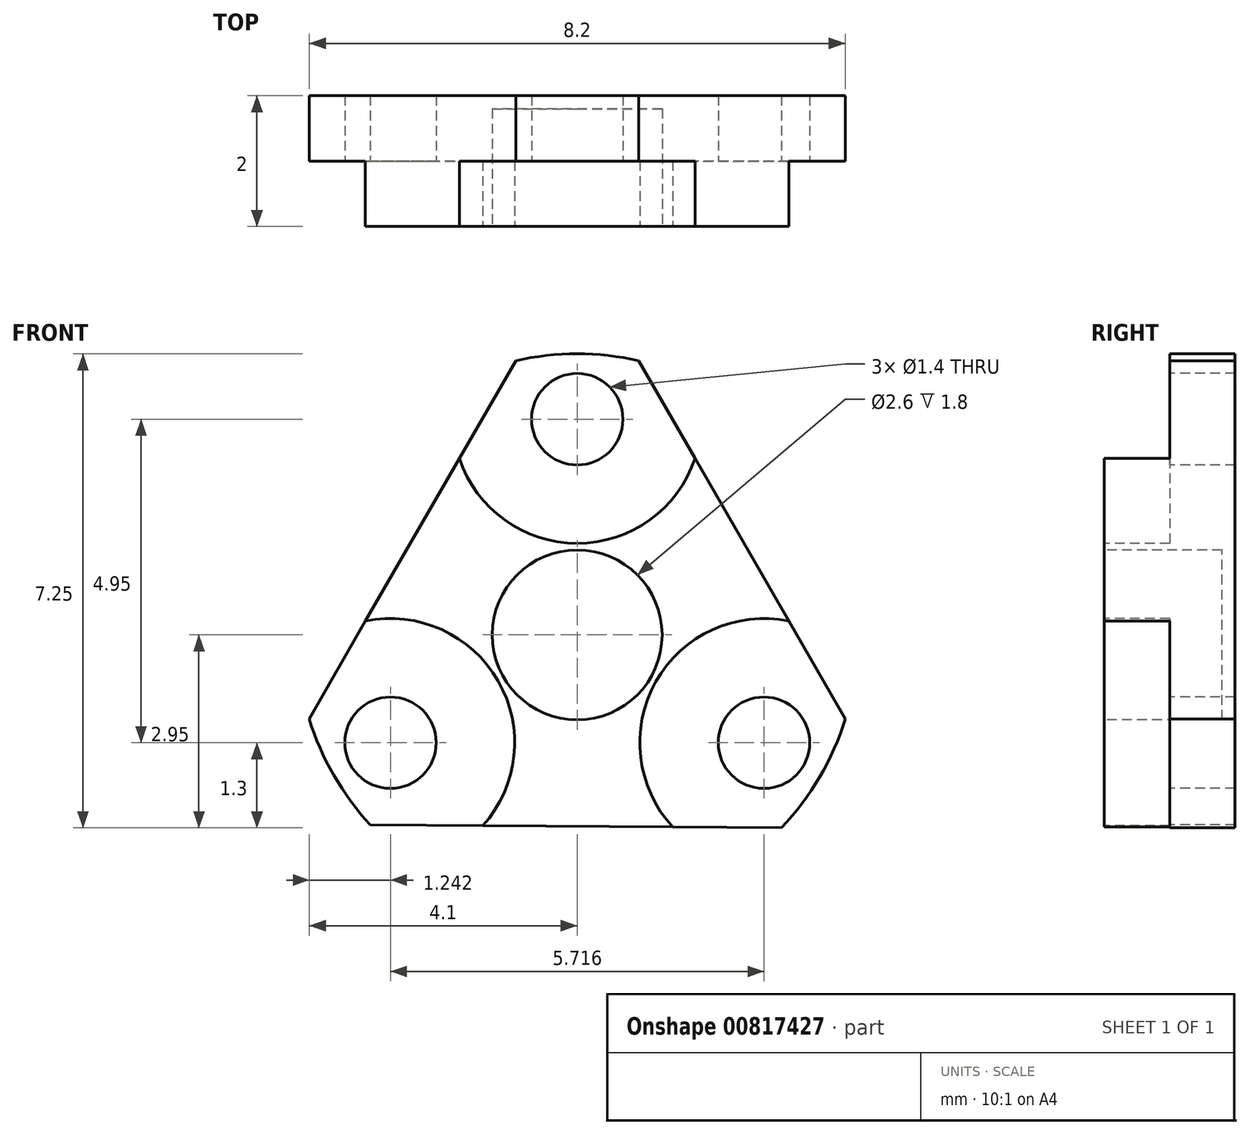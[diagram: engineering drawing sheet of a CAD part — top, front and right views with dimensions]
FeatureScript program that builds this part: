
annotation { "Feature Type Name" : "Feature", "Feature Type Description" : "" }
export const myFeature = defineFeature(function(context is Context, id is Id, definition is map)
    precondition{}
    {
        {
            var Q0;
            Q0=qCreatedBy(makeId("Front.planeOp"),FACE);
            var sketch = newSketch(context, id + "F0", { "sketchPlane" : qUnion([Q0])});
            skCircle(sketch, "E0", {"center": v(0, 0) * mm, "radius": 4.3 * mm});
            skSolve(sketch);
        }
        {
            var Q0;
            Q0=makeQuery(id+"F0.imprint","IMPRINT",FACE,{"disambiguationData":[TD([[makeQuery(id+"F0.imprint","IMPRINT",EDGE,{"derivedFrom":sQuery(id+"F0.wireOp",EDGE,"E0")}),1.0]])]});
            extrude(context, id + "F1", {"entities" : qUnion([Q0]), "depth" : 2 * mm, "offsetDistance" : 25 * mm});
        }
        {
            var Q0;
            Q0=makeQuery(id+"F1.opExtrude","CAP_FACE",FACE,{"disambiguationData":[OSD([sQuery(id+"F0.wireOp",EDGE,"E0")])],"isStart":false});
            var sketch = newSketch(context, id + "F2", { "sketchPlane" : qUnion([Q0])});
            skCircle(sketch, "E1", {"center": v(0, 3.3) * mm, "radius": 1.9 * mm});
            skCircle(sketch, "E2", {"center": v(0, 3.3) * mm, "radius": 0.7 * mm});
            skPoint(sketch, "E3.center", {"position": v(0, 0) * mm});
            skCircle(sketch, "E4.1.0", {"center": v(-2.86, -1.65) * mm, "radius": 0.7 * mm});
            skCircle(sketch, "E4.1.1", {"center": v(-2.86, -1.65) * mm, "radius": 1.9 * mm});
            skCircle(sketch, "E4.2.0", {"center": v(2.86, -1.65) * mm, "radius": 0.7 * mm});
            skCircle(sketch, "E4.2.1", {"center": v(2.86, -1.65) * mm, "radius": 1.9 * mm});
            skLineSegment(sketch, "E5", {"start": v(4.28, -0.4) * mm, "end": v(1.8, 3.9) * mm, "construction": true});
            skLineSegment(sketch, "E6", {"start": v(-2.48, -3.51) * mm, "end": v(2.43, -3.55) * mm, "construction": true});
            skLineSegment(sketch, "E7", {"start": v(-4.28, -0.4) * mm, "end": v(-1.8, 3.9) * mm, "construction": true});
            skLineSegment(sketch, "E8.0", {"start": v(-4.1, -1.28) * mm, "end": v(-0.94, 4.2) * mm});
            skLineSegment(sketch, "E9.0", {"start": v(-3.17, -2.9) * mm, "end": v(3.13, -2.95) * mm});
            skLineSegment(sketch, "E10.0", {"start": v(4.1, -1.28) * mm, "end": v(0.94, 4.2) * mm});
            skSolve(sketch);
        }
        {
            var Q0;
            Q0=makeQuery(id+"F2.imprint","IMPRINT",FACE,{"disambiguationData":[TD([[makeQuery(id+"F2.imprint","IMPRINT",EDGE,{"derivedFrom":sQuery(id+"F2.wireOp",EDGE,"E4.1.0")}),-1.0]])]});
            var Q1;
            Q1=makeQuery(id+"F2.imprint","IMPRINT",FACE,{"disambiguationData":[TD([[makeQuery(id+"F2.imprint","IMPRINT",EDGE,{"derivedFrom":sQuery(id+"F2.wireOp",EDGE,"E4.2.0")}),-1.0]])]});
            var Q2;
            Q2=makeQuery(id+"F2.imprint","IMPRINT",FACE,{"disambiguationData":[TD([[makeQuery(id+"F2.imprint","IMPRINT",EDGE,{"derivedFrom":sQuery(id+"F2.wireOp",EDGE,"E2")}),-1.0]])]});
            extrude(context, id + "F3", {"entities" : qUnion([Q0, Q1, Q2]), "operationType" : NewBodyOperationType.REMOVE, "oppositeDirection" : true, "depth" : 1 * mm, "offsetDistance" : 25 * mm});
        }
        {
            var Q0;
            Q0=makeQuery(id+"F3.boolean.opBoolean","SPLIT",FACE,{"disambiguationData":[TD([makeQuery(id+"F3.opExtrude","SWEPT_FACE",FACE,{"disambiguationData":[OSD([sQuery(id+"F2.wireOp",EDGE,"E2")])]})])],"derivedFrom":makeQuery(id+"F1.opExtrude","CAP_FACE",FACE,{"disambiguationData":[OSD([sQuery(id+"F0.wireOp",EDGE,"E0")])],"isStart":false})});
            var Q1;
            Q1=makeQuery(id+"F3.boolean.opBoolean","SPLIT",FACE,{"disambiguationData":[TD([makeQuery(id+"F3.opExtrude","SWEPT_FACE",FACE,{"disambiguationData":[OSD([sQuery(id+"F2.wireOp",EDGE,"E4.1.0")])]})])],"derivedFrom":makeQuery(id+"F1.opExtrude","CAP_FACE",FACE,{"disambiguationData":[OSD([sQuery(id+"F0.wireOp",EDGE,"E0")])],"isStart":false})});
            var Q2;
            Q2=makeQuery(id+"F3.boolean.opBoolean","SPLIT",FACE,{"disambiguationData":[TD([makeQuery(id+"F3.opExtrude","SWEPT_FACE",FACE,{"disambiguationData":[OSD([sQuery(id+"F2.wireOp",EDGE,"E4.2.0")])]})])],"derivedFrom":makeQuery(id+"F1.opExtrude","CAP_FACE",FACE,{"disambiguationData":[OSD([sQuery(id+"F0.wireOp",EDGE,"E0")])],"isStart":false})});
            extrude(context, id + "F4", {"entities" : qUnion([Q0, Q1, Q2]), "operationType" : NewBodyOperationType.REMOVE, "oppositeDirection" : true, "depth" : 2 * mm, "offsetDistance" : 25 * mm});
        }
        {
            var Q0;
            {var subQ0=sQuery(id+"F0.wireOp",EDGE,"E0");Q0=makeQuery(id+"F3.boolean.opBoolean","SPLIT",FACE,{"disambiguationData":[TD([makeQuery(id+"F1.opExtrude","SWEPT_FACE",FACE,{"disambiguationData":[OSD([subQ0])]})])],"derivedFrom":makeQuery(id+"F1.opExtrude","CAP_FACE",FACE,{"disambiguationData":[OSD([subQ0])],"isStart":false})});}
            var sketch = newSketch(context, id + "F5", { "sketchPlane" : qUnion([Q0])});
            skCircle(sketch, "E11", {"center": v(0, 0) * mm, "radius": 1.3 * mm});
            skSolve(sketch);
        }
        {
            var Q0;
            Q0=makeQuery(id+"F5.imprint","IMPRINT",FACE,{"disambiguationData":[TD([[makeQuery(id+"F5.imprint","IMPRINT",EDGE,{"derivedFrom":sQuery(id+"F5.wireOp",EDGE,"E11")}),1.0]])]});
            extrude(context, id + "F6", {"entities" : qUnion([Q0]), "operationType" : NewBodyOperationType.REMOVE, "oppositeDirection" : true, "depth" : 1.8 * mm, "offsetDistance" : 25 * mm});
        }
        {
            var Q0;
            {var subQ0=sQuery(id+"F2.wireOp",EDGE,"E10.0");var subQ1=sQuery(id+"F2.wireOp",EDGE,"E1");var subQ2=makeQuery(id+"F2.imprint","INTERSECT",VERTEX,{"derivedFrom":[subQ1,subQ0]});Q0=makeQuery(id+"F2.imprint","IMPRINT",FACE,{"disambiguationData":[TD([[makeQuery(id+"F2.imprint","IMPRINT",EDGE,{"disambiguationData":[TD([[subQ2,-1.0]])],"derivedFrom":subQ1}),-1.0]])]});}
            var Q1;
            {var subQ0=sQuery(id+"F2.wireOp",EDGE,"E10.0");var subQ1=sQuery(id+"F2.wireOp",EDGE,"E1");var subQ2=makeQuery(id+"F2.imprint","INTERSECT",VERTEX,{"derivedFrom":[subQ1,subQ0]});Q1=makeQuery(id+"F2.imprint","IMPRINT",FACE,{"disambiguationData":[TD([[makeQuery(id+"F2.imprint","IMPRINT",EDGE,{"disambiguationData":[TD([[subQ2,-1.0]])],"derivedFrom":subQ1}),1.0]])]});}
            var Q2;
            {var subQ0=sQuery(id+"F2.wireOp",EDGE,"E10.0");var subQ1=sQuery(id+"F2.wireOp",EDGE,"E4.2.1");var subQ2=makeQuery(id+"F2.imprint","INTERSECT",VERTEX,{"derivedFrom":[subQ1,subQ0]});Q2=makeQuery(id+"F2.imprint","IMPRINT",FACE,{"disambiguationData":[TD([[makeQuery(id+"F2.imprint","IMPRINT",EDGE,{"disambiguationData":[TD([[subQ2,1.0]])],"derivedFrom":subQ1}),1.0]])]});}
            var Q3;
            {var subQ0=sQuery(id+"F2.wireOp",EDGE,"E8.0");var subQ1=sQuery(id+"F2.wireOp",EDGE,"E1");var subQ2=makeQuery(id+"F2.imprint","INTERSECT",VERTEX,{"derivedFrom":[subQ1,subQ0]});Q3=makeQuery(id+"F2.imprint","IMPRINT",FACE,{"disambiguationData":[TD([[makeQuery(id+"F2.imprint","IMPRINT",EDGE,{"disambiguationData":[TD([[subQ2,1.0]])],"derivedFrom":subQ1}),-1.0]])]});}
            var Q4;
            {var subQ0=sQuery(id+"F2.wireOp",EDGE,"E8.0");var subQ1=sQuery(id+"F2.wireOp",EDGE,"E1");var subQ2=makeQuery(id+"F2.imprint","INTERSECT",VERTEX,{"derivedFrom":[subQ1,subQ0]});Q4=makeQuery(id+"F2.imprint","IMPRINT",FACE,{"disambiguationData":[TD([[makeQuery(id+"F2.imprint","IMPRINT",EDGE,{"disambiguationData":[TD([[subQ2,1.0]])],"derivedFrom":subQ1}),1.0]])]});}
            var Q5;
            {var subQ0=sQuery(id+"F2.wireOp",EDGE,"E8.0");var subQ1=sQuery(id+"F2.wireOp",EDGE,"E4.1.1");var subQ2=makeQuery(id+"F2.imprint","INTERSECT",VERTEX,{"derivedFrom":[subQ1,subQ0]});Q5=makeQuery(id+"F2.imprint","IMPRINT",FACE,{"disambiguationData":[TD([[makeQuery(id+"F2.imprint","IMPRINT",EDGE,{"disambiguationData":[TD([[subQ2,-1.0]])],"derivedFrom":subQ1}),1.0]])]});}
            var Q6;
            {var subQ0=sQuery(id+"F2.wireOp",EDGE,"E9.0");var subQ1=sQuery(id+"F2.wireOp",EDGE,"E4.1.1");var subQ2=makeQuery(id+"F2.imprint","INTERSECT",VERTEX,{"derivedFrom":[subQ1,subQ0]});Q6=makeQuery(id+"F2.imprint","IMPRINT",FACE,{"disambiguationData":[TD([[makeQuery(id+"F2.imprint","IMPRINT",EDGE,{"disambiguationData":[TD([[subQ2,1.0]])],"derivedFrom":subQ1}),1.0]])]});}
            var Q7;
            {var subQ0=sQuery(id+"F2.wireOp",EDGE,"E9.0");var subQ1=sQuery(id+"F2.wireOp",EDGE,"E4.1.1");var subQ2=makeQuery(id+"F2.imprint","INTERSECT",VERTEX,{"derivedFrom":[subQ1,subQ0]});Q7=makeQuery(id+"F2.imprint","IMPRINT",FACE,{"disambiguationData":[TD([[makeQuery(id+"F2.imprint","IMPRINT",EDGE,{"disambiguationData":[TD([[subQ2,1.0]])],"derivedFrom":subQ1}),-1.0]])]});}
            var Q8;
            {var subQ0=sQuery(id+"F2.wireOp",EDGE,"E9.0");var subQ1=sQuery(id+"F2.wireOp",EDGE,"E4.2.1");var subQ2=makeQuery(id+"F2.imprint","INTERSECT",VERTEX,{"derivedFrom":[subQ1,subQ0]});Q8=makeQuery(id+"F2.imprint","IMPRINT",FACE,{"disambiguationData":[TD([[makeQuery(id+"F2.imprint","IMPRINT",EDGE,{"disambiguationData":[TD([[subQ2,-1.0]])],"derivedFrom":subQ1}),1.0]])]});}
            extrude(context, id + "F7", {"entities" : qUnion([Q0, Q1, Q2, Q3, Q4, Q5, Q6, Q7, Q8]), "operationType" : NewBodyOperationType.REMOVE, "oppositeDirection" : true, "depth" : 2 * mm, "offsetDistance" : 25 * mm});
        }
    });
